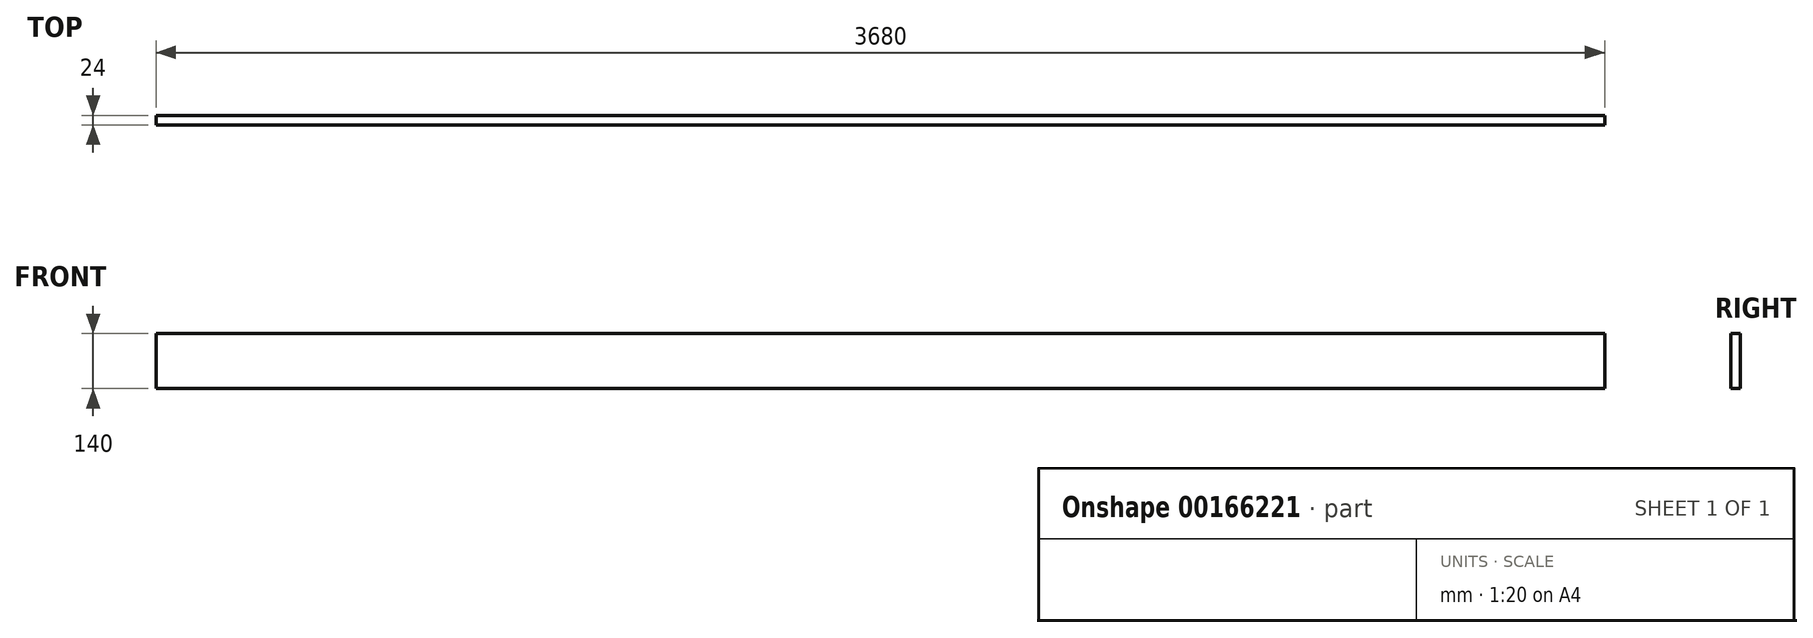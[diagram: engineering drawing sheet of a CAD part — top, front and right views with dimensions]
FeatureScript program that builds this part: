
annotation { "Feature Type Name" : "Feature", "Feature Type Description" : "" }
export const myFeature = defineFeature(function(context is Context, id is Id, definition is map)
    precondition{}
    {
        {
            var Q0;
            Q0=qCreatedBy(makeId("Front.planeOp"),FACE);
            var sketch = newSketch(context, id + "F0", { "sketchPlane" : qUnion([Q0])});
            skLineSegment(sketch, "E0.bottom", {"start": v(-1840, -70) * mm, "end": v(1840, -70) * mm});
            skLineSegment(sketch, "E0.top", {"start": v(-1840, 70) * mm, "end": v(1840, 70) * mm});
            skLineSegment(sketch, "E0.left", {"start": v(-1840, -70) * mm, "end": v(-1840, 70) * mm});
            skLineSegment(sketch, "E0.right", {"start": v(1840, -70) * mm, "end": v(1840, 70) * mm});
            skPoint(sketch, "E0.middle", {"position": v(0, 0) * mm});
            skSolve(sketch);
        }
        {
            var Q0;
            Q0=makeQuery(id+"F0.imprint","IMPRINT",FACE,{"disambiguationData":[TD([[makeQuery(id+"F0.imprint","IMPRINT",EDGE,{"derivedFrom":sQuery(id+"F0.wireOp",EDGE,"E0.bottom")}),1.0]])]});
            extrude(context, id + "F1", {"entities" : qUnion([Q0]), "depth" : 24 * mm, "symmetric" : true});
        }
    });
